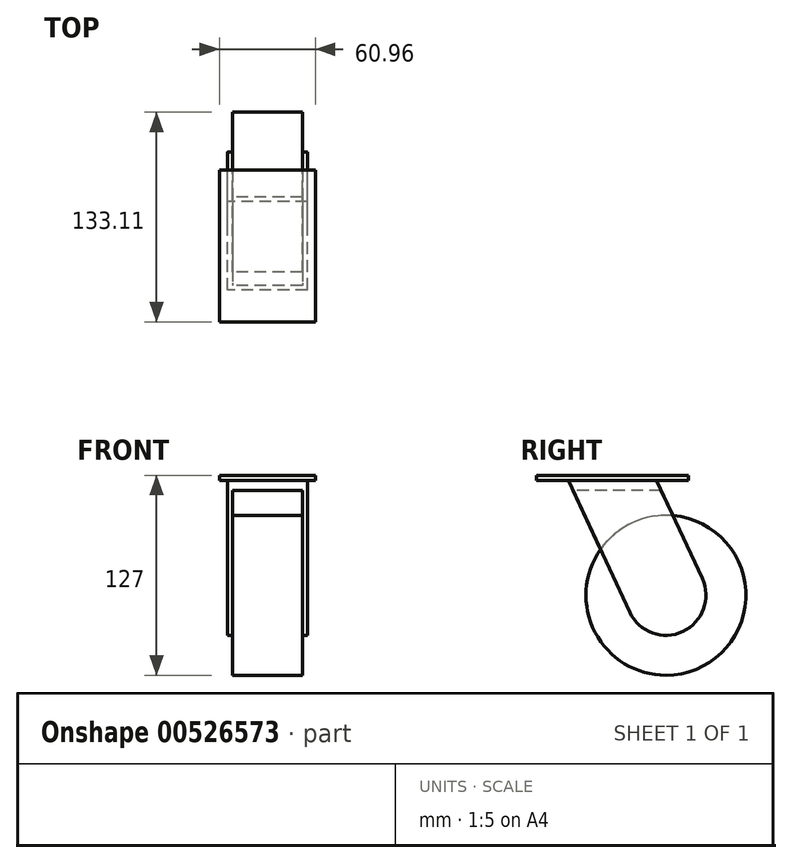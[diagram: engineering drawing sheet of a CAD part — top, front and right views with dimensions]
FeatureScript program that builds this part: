
annotation { "Feature Type Name" : "Feature", "Feature Type Description" : "" }
export const myFeature = defineFeature(function(context is Context, id is Id, definition is map)
    precondition{}
    {
        {
            var Q0;
            Q0=qCreatedBy(makeId("Top.planeOp"),FACE);
            var sketch = newSketch(context, id + "F0", { "sketchPlane" : qUnion([Q0])});
            skLineSegment(sketch, "E0.bottom", {"start": v(-30.48, 48.26) * mm, "end": v(30.48, 48.26) * mm});
            skLineSegment(sketch, "E0.top", {"start": v(-30.48, -48.26) * mm, "end": v(30.48, -48.26) * mm});
            skLineSegment(sketch, "E0.left", {"start": v(-30.48, 48.26) * mm, "end": v(-30.48, -48.26) * mm});
            skLineSegment(sketch, "E0.right", {"start": v(30.48, 48.26) * mm, "end": v(30.48, -48.26) * mm});
            skPoint(sketch, "E0.middle", {"position": v(0, 0) * mm});
            skSolve(sketch);
        }
        {
            var Q0;
            Q0 = qSketchRegion(id + "F0", true);
            extrude(context, id + "F1", {"entities" : qUnion([Q0]), "oppositeDirection" : true, "depth" : 3.17 * mm, "offsetDistance" : 25.4 * mm});
        }
        {
            var Q0;
            Q0=qCreatedBy(makeId("Right.planeOp"),FACE);
            var sketch = newSketch(context, id + "F2", { "sketchPlane" : qUnion([Q0])});
            skCircle(sketch, "E1", {"center": v(34.05, -76.2) * mm, "radius": 50.8 * mm});
            skLineSegment(sketch, "E2", {"start": v(34.05, -127) * mm, "end": v(129.52, -127) * mm});
            skLineSegment(sketch, "E3", {"start": v(-28.03, -3.18) * mm, "end": v(28.03, -3.18) * mm});
            skLineSegment(sketch, "E4", {"start": v(28.03, -3.17) * mm, "end": v(57.07, -65.47) * mm});
            skLineSegment(sketch, "E5", {"start": v(-28.03, -3.17) * mm, "end": v(11.03, -86.93) * mm});
            skArc(sketch, "E6", {"start": v(11.03, -86.93) * mm, "mid": v(44.79, -99.22) * mm, "end": v(57.07, -65.47) * mm});
            skLineSegment(sketch, "E7", {"start": v(0, -3.18) * mm, "end": v(0, 0) * mm, "construction": true});
            skSolve(sketch);
        }
        {
            var Q0;
            {var subQ5=sQuery(id+"F2.wireOp",EDGE,"E3");Q0=makeQuery(id+"F2.imprint","IMPRINT",FACE,{"disambiguationData":[TD([[makeQuery(id+"F2.imprint","IMPRINT",EDGE,{"derivedFrom":subQ5}),-1.0]])]});}
            var Q1;
            {var subQ5=sQuery(id+"F2.wireOp",EDGE,"E6");Q1=makeQuery(id+"F2.imprint","IMPRINT",FACE,{"disambiguationData":[TD([[makeQuery(id+"F2.imprint","IMPRINT",EDGE,{"derivedFrom":subQ5}),1.0]])]});}
            extrude(context, id + "F3", {"entities" : qUnion([Q0, Q1]), "operationType" : NewBodyOperationType.ADD, "endBound" : BoundingType.SYMMETRIC, "depth" : 50.8 * mm, "offsetDistance" : 25.4 * mm});
        }
        {
            var Q0;
            Q0=makeQuery(id+"F1.opExtrude","SWEPT_FACE",FACE,{"disambiguationData":[OSD([sQuery(id+"F0.wireOp",EDGE,"E0.top")])]});
            var sketch = newSketch(context, id + "F4", { "sketchPlane" : qUnion([Q0])});
            skLineSegment(sketch, "E8.top", {"start": v(-22.22, -111.13) * mm, "end": v(22.23, -111.12) * mm});
            skLineSegment(sketch, "E8.left", {"start": v(-22.23, -9.52) * mm, "end": v(-22.23, -111.13) * mm});
            skLineSegment(sketch, "E8.right", {"start": v(22.22, -9.52) * mm, "end": v(22.23, -111.12) * mm});
            skLineSegment(sketch, "E9", {"start": v(-22.23, -9.53) * mm, "end": v(22.22, -9.53) * mm});
            skSolve(sketch);
        }
        {
            var Q0;
            Q0 = qSketchRegion(id + "F4", true);
            extrude(context, id + "F5", {"entities" : qUnion([Q0]), "operationType" : NewBodyOperationType.REMOVE, "endBound" : BoundingType.THROUGH_ALL, "oppositeDirection" : true, "depth" : 25.4 * mm, "offsetDistance" : 25.4 * mm});
        }
        {
            var Q0;
            {var subQ0=sQuery(id+"F2.wireOp",EDGE,"E6");Q0=makeQuery(id+"F2.imprint","IMPRINT",FACE,{"disambiguationData":[TD([[makeQuery(id+"F2.imprint","IMPRINT",EDGE,{"derivedFrom":subQ0}),-1.0]])]});}
            var Q1;
            {var subQ5=sQuery(id+"F2.wireOp",EDGE,"E6");Q1=makeQuery(id+"F2.imprint","IMPRINT",FACE,{"disambiguationData":[TD([[makeQuery(id+"F2.imprint","IMPRINT",EDGE,{"derivedFrom":subQ5}),1.0]])]});}
            extrude(context, id + "F6", {"entities" : qUnion([Q0, Q1]), "endBound" : BoundingType.SYMMETRIC, "depth" : 44.45 * mm, "offsetDistance" : 25.4 * mm});
        }
    });
